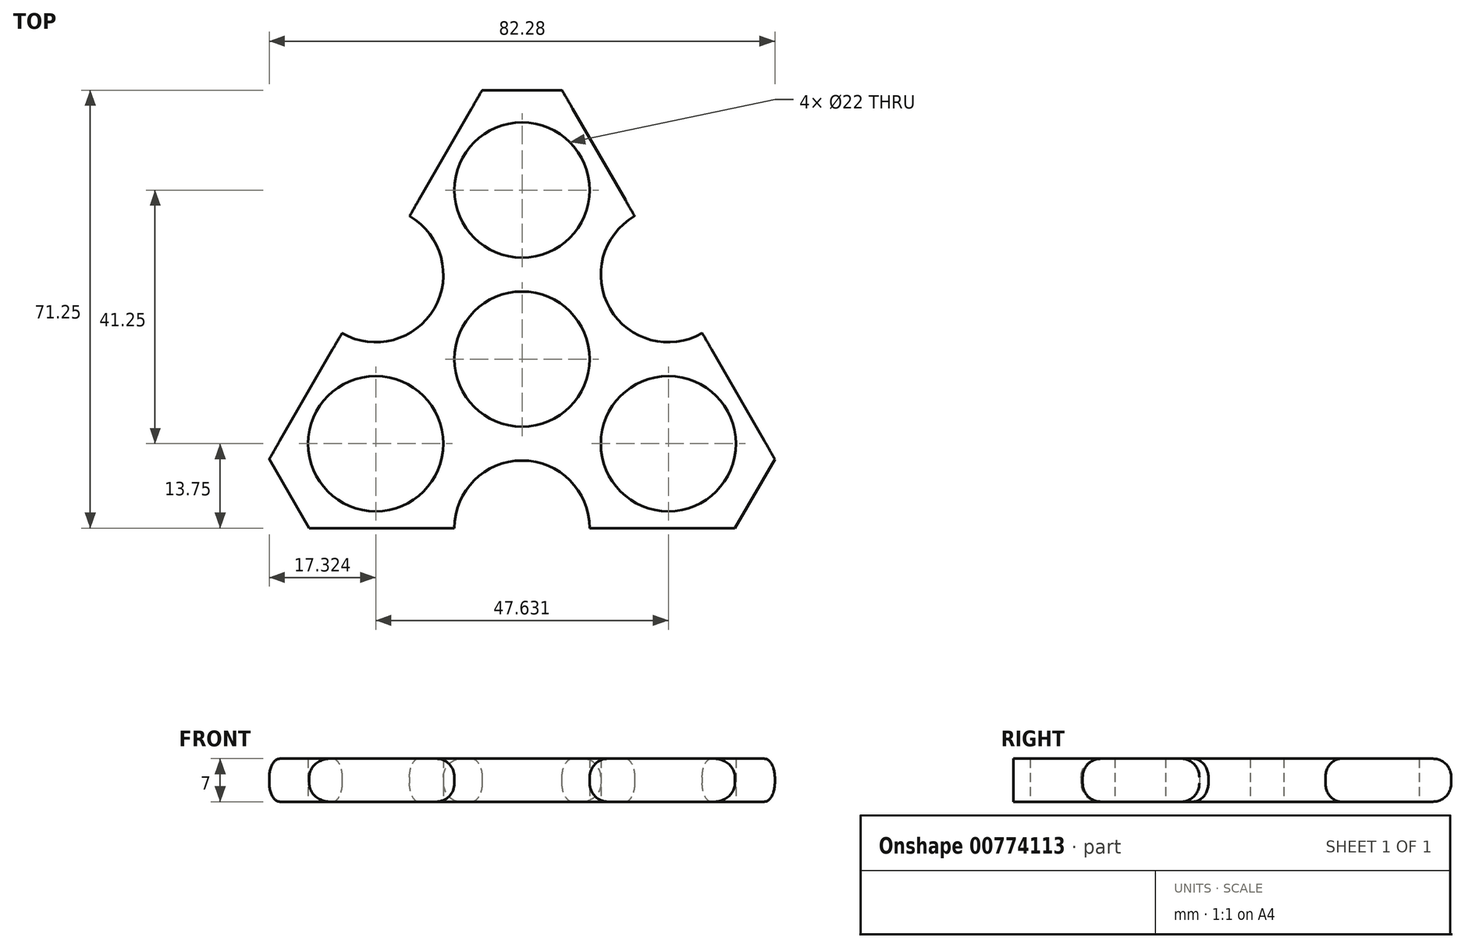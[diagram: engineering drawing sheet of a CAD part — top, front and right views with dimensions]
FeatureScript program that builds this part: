
annotation { "Feature Type Name" : "Feature", "Feature Type Description" : "" }
export const myFeature = defineFeature(function(context is Context, id is Id, definition is map)
    precondition{}
    {
        {
            var Q0;
            Q0=qCreatedBy(makeId("Top.planeOp"),FACE);
            var sketch = newSketch(context, id + "F0", { "sketchPlane" : qUnion([Q0])});
            skPoint(sketch, "E0", {"position": v(0, 0) * mm});
            skCircle(sketch, "E1", {"center": v(0, 0) * mm, "radius": 11 * mm});
            skCircle(sketch, "E2.cCircle", {"center": v(0, 0) * mm, "radius": 27.5 * mm, "construction": true});
            skLineSegment(sketch, "E2.0", {"start": v(47.63, -27.5) * mm, "end": v(-47.63, -27.5) * mm});
            skLineSegment(sketch, "E2.1", {"start": v(-47.63, -27.5) * mm, "end": v(0, 55) * mm});
            skLineSegment(sketch, "E2.2", {"start": v(0, 55) * mm, "end": v(47.63, -27.5) * mm});
            skPoint(sketch, "E2.0.midPoint", {"position": v(0, -27.5) * mm});
            skLineSegment(sketch, "E3", {"start": v(-47.63, -27.5) * mm, "end": v(0, 0) * mm});
            skLineSegment(sketch, "E4", {"start": v(0, 0) * mm, "end": v(47.63, -27.5) * mm});
            skLineSegment(sketch, "E5", {"start": v(0, 0) * mm, "end": v(0, 55) * mm});
            skCircle(sketch, "E6", {"center": v(-23.82, 13.75) * mm, "radius": 11 * mm});
            skCircle(sketch, "E7", {"center": v(23.82, 13.75) * mm, "radius": 11 * mm});
            skCircle(sketch, "E8", {"center": v(0, -27.5) * mm, "radius": 11 * mm});
            skPoint(sketch, "E9", {"position": v(23.82, -13.75) * mm});
            skPoint(sketch, "E10", {"position": v(0, 27.5) * mm});
            skPoint(sketch, "E11", {"position": v(-23.82, -13.75) * mm});
            skCircle(sketch, "E12", {"center": v(-23.82, -13.75) * mm, "radius": 11 * mm});
            skCircle(sketch, "E13", {"center": v(23.82, -13.75) * mm, "radius": 11 * mm});
            skCircle(sketch, "E14", {"center": v(0, 27.5) * mm, "radius": 11 * mm});
            skSolve(sketch);
        }
        {
            var Q0;
            {var subQ8=sQuery(id+"F0.wireOp",EDGE,"E3");var subQ11=sQuery(id+"F0.wireOp",EDGE,"E1");var subQ12=makeQuery(id+"F0.imprint","INTERSECT",VERTEX,{"derivedFrom":[subQ11,subQ8]});Q0=makeQuery(id+"F0.imprint","IMPRINT",FACE,{"disambiguationData":[TD([[makeQuery(id+"F0.imprint","IMPRINT",EDGE,{"disambiguationData":[TD([[subQ12,1.0]])],"derivedFrom":subQ11}),-1.0]])]});}
            var Q1;
            {var subQ0=sQuery(id+"F0.wireOp",EDGE,"E5");var subQ4=sQuery(id+"F0.wireOp",EDGE,"E1");var subQ5=makeQuery(id+"F0.imprint","INTERSECT",VERTEX,{"derivedFrom":[subQ4,subQ0]});Q1=makeQuery(id+"F0.imprint","IMPRINT",FACE,{"disambiguationData":[TD([[makeQuery(id+"F0.imprint","IMPRINT",EDGE,{"disambiguationData":[TD([[subQ5,1.0]])],"derivedFrom":subQ4}),-1.0]])]});}
            var Q2;
            {var subQ8=sQuery(id+"F0.wireOp",EDGE,"E3");var subQ11=sQuery(id+"F0.wireOp",EDGE,"E1");var subQ12=makeQuery(id+"F0.imprint","INTERSECT",VERTEX,{"derivedFrom":[subQ11,subQ8]});Q2=makeQuery(id+"F0.imprint","IMPRINT",FACE,{"disambiguationData":[TD([[makeQuery(id+"F0.imprint","IMPRINT",EDGE,{"disambiguationData":[TD([[subQ12,-1.0]])],"derivedFrom":subQ11}),-1.0]])]});}
            extrude(context, id + "F1", {"entities" : qUnion([Q0, Q1, Q2]), "depth" : 3.5 * mm, "offsetDistance" : 25 * mm, "hasSecondDirection" : true, "secondDirectionOppositeDirection" : true, "secondDirectionDepth" : 3.5 * mm});
        }
        {
            var Q0;
            Q0=makeQuery(id+"F1.opExtrude","SWEPT_EDGE",EDGE,{"disambiguationData":[OSD([sQuery(id+"F0.wireOp",EDGE,"E2.1"),sQuery(id+"F0.wireOp",EDGE,"E2.2"),sQuery(id+"F0.wireOp",EDGE,"E5")])]});
            var Q1;
            Q1=makeQuery(id+"F1.opExtrude","SWEPT_EDGE",EDGE,{"disambiguationData":[OSD([sQuery(id+"F0.wireOp",EDGE,"E2.0"),sQuery(id+"F0.wireOp",EDGE,"E2.2"),sQuery(id+"F0.wireOp",EDGE,"E4")])]});
            var Q2;
            Q2=makeQuery(id+"F1.opExtrude","SWEPT_EDGE",EDGE,{"disambiguationData":[OSD([sQuery(id+"F0.wireOp",EDGE,"E2.0"),sQuery(id+"F0.wireOp",EDGE,"E2.1"),sQuery(id+"F0.wireOp",EDGE,"E3")])]});
            chamfer(context, id + "F2", {"entities" : qUnion([Q0, Q1, Q2]), "width" : 7.5 * mm, "tangentPropagation" : true});
        }
        {
            var Q0;
            {var subQ0=sQuery(id+"F0.wireOp",EDGE,"E2.2");Q0=makeQuery(id+"F1.opExtrude","CAP_EDGE",EDGE,{"disambiguationData":[OSD([subQ0]),TDD([makeQuery(id+"F0.imprint","IMPRINT",EDGE,{"disambiguationData":[TD([[makeQuery(id+"F0.imprint","INTERSECT",VERTEX,{"disambiguationData":[OD(0.0)],"derivedFrom":[subQ0,sQuery(id+"F0.wireOp",EDGE,"E7")]}),1.0]])],"derivedFrom":subQ0})])],"isStart":false});}
            var Q1;
            Q1=makeQuery(id+"F1.opExtrude","CAP_EDGE",EDGE,{"disambiguationData":[OSD([sQuery(id+"F0.wireOp",EDGE,"E7")])],"isStart":false});
            var Q2;
            {var subQ0=sQuery(id+"F0.wireOp",EDGE,"E2.2");Q2=makeQuery(id+"F1.opExtrude","CAP_EDGE",EDGE,{"disambiguationData":[OSD([subQ0]),TDD([makeQuery(id+"F0.imprint","IMPRINT",EDGE,{"disambiguationData":[TD([[makeQuery(id+"F0.imprint","INTERSECT",VERTEX,{"disambiguationData":[OD(1.0)],"derivedFrom":[subQ0,sQuery(id+"F0.wireOp",EDGE,"E7")]}),-1.0]])],"derivedFrom":subQ0})])],"isStart":false});}
            var Q3;
            {var subQ0=sQuery(id+"F0.wireOp",EDGE,"E2.2");var subQ1=sQuery(id+"F0.wireOp",EDGE,"E2.0");Q3=makeQuery(id+"F2.opChamfer","BLEND_EDGE",EDGE,{"blendedFrom":[makeQuery(id+"F1.opExtrude","SWEPT_EDGE",EDGE,{"disambiguationData":[OSD([subQ1,subQ0,sQuery(id+"F0.wireOp",EDGE,"E4")])]}),makeQuery(id+"F1.opExtrude","CAP_FACE",FACE,{"disambiguationData":[OSD([sQuery(id+"F0.wireOp",EDGE,"E1"),subQ1,sQuery(id+"F0.wireOp",EDGE,"E2.1"),subQ0,sQuery(id+"F0.wireOp",EDGE,"E6"),sQuery(id+"F0.wireOp",EDGE,"E7"),sQuery(id+"F0.wireOp",EDGE,"E8"),sQuery(id+"F0.wireOp",EDGE,"eb86181a-66c7-44a9-927e-2462891ccdc7.0"),sQuery(id+"F0.wireOp",EDGE,"eb86181a-66c7-44a9-927e-2462891ccdc7.1"),sQuery(id+"F0.wireOp",EDGE,"eb86181a-66c7-44a9-927e-2462891ccdc7.2"),sQuery(id+"F0.wireOp",EDGE,"eb86181a-66c7-44a9-927e-2462891ccdc7.3"),sQuery(id+"F0.wireOp",EDGE,"eb86181a-66c7-44a9-927e-2462891ccdc7.4"),sQuery(id+"F0.wireOp",EDGE,"eb86181a-66c7-44a9-927e-2462891ccdc7.5"),sQuery(id+"F0.wireOp",EDGE,"eff1ef34-f5c1-4426-bce6-d10491bb5129.0"),sQuery(id+"F0.wireOp",EDGE,"eff1ef34-f5c1-4426-bce6-d10491bb5129.1"),sQuery(id+"F0.wireOp",EDGE,"eff1ef34-f5c1-4426-bce6-d10491bb5129.2"),sQuery(id+"F0.wireOp",EDGE,"eff1ef34-f5c1-4426-bce6-d10491bb5129.3"),sQuery(id+"F0.wireOp",EDGE,"eff1ef34-f5c1-4426-bce6-d10491bb5129.4"),sQuery(id+"F0.wireOp",EDGE,"eff1ef34-f5c1-4426-bce6-d10491bb5129.5"),sQuery(id+"F0.wireOp",EDGE,"caa0a2bf-8681-4059-bf23-da4b8e81c40b0.MirrorCS"),sQuery(id+"F0.wireOp",EDGE,"1fd086fe-55f3-407d-936a-1a1085770df10.MirrorCS"),sQuery(id+"F0.wireOp",EDGE,"178d0676-7881-4249-8293-cbce84a7fd370.MirrorCS"),sQuery(id+"F0.wireOp",EDGE,"88477509-62b1-4317-9a81-a130adc69aff0.MirrorCS"),sQuery(id+"F0.wireOp",EDGE,"1c665bfd-ff3e-46d6-9b43-bc498a36d9eb0.MirrorCS"),sQuery(id+"F0.wireOp",EDGE,"5c9001ee-5b7d-4471-8c19-4e4f09c0f1da0.MirrorCS")])],"isStart":false})],"blendedInto":[makeQuery(id+"F1.opExtrude","CAP_FACE",FACE,{"disambiguationData":[OSD([sQuery(id+"F0.wireOp",EDGE,"E1"),subQ1,sQuery(id+"F0.wireOp",EDGE,"E2.1"),subQ0,sQuery(id+"F0.wireOp",EDGE,"E6"),sQuery(id+"F0.wireOp",EDGE,"E7"),sQuery(id+"F0.wireOp",EDGE,"E8"),sQuery(id+"F0.wireOp",EDGE,"eb86181a-66c7-44a9-927e-2462891ccdc7.0"),sQuery(id+"F0.wireOp",EDGE,"eb86181a-66c7-44a9-927e-2462891ccdc7.1"),sQuery(id+"F0.wireOp",EDGE,"eb86181a-66c7-44a9-927e-2462891ccdc7.2"),sQuery(id+"F0.wireOp",EDGE,"eb86181a-66c7-44a9-927e-2462891ccdc7.3"),sQuery(id+"F0.wireOp",EDGE,"eb86181a-66c7-44a9-927e-2462891ccdc7.4"),sQuery(id+"F0.wireOp",EDGE,"eb86181a-66c7-44a9-927e-2462891ccdc7.5"),sQuery(id+"F0.wireOp",EDGE,"eff1ef34-f5c1-4426-bce6-d10491bb5129.0"),sQuery(id+"F0.wireOp",EDGE,"eff1ef34-f5c1-4426-bce6-d10491bb5129.1"),sQuery(id+"F0.wireOp",EDGE,"eff1ef34-f5c1-4426-bce6-d10491bb5129.2"),sQuery(id+"F0.wireOp",EDGE,"eff1ef34-f5c1-4426-bce6-d10491bb5129.3"),sQuery(id+"F0.wireOp",EDGE,"eff1ef34-f5c1-4426-bce6-d10491bb5129.4"),sQuery(id+"F0.wireOp",EDGE,"eff1ef34-f5c1-4426-bce6-d10491bb5129.5"),sQuery(id+"F0.wireOp",EDGE,"caa0a2bf-8681-4059-bf23-da4b8e81c40b0.MirrorCS"),sQuery(id+"F0.wireOp",EDGE,"1fd086fe-55f3-407d-936a-1a1085770df10.MirrorCS"),sQuery(id+"F0.wireOp",EDGE,"178d0676-7881-4249-8293-cbce84a7fd370.MirrorCS"),sQuery(id+"F0.wireOp",EDGE,"88477509-62b1-4317-9a81-a130adc69aff0.MirrorCS"),sQuery(id+"F0.wireOp",EDGE,"1c665bfd-ff3e-46d6-9b43-bc498a36d9eb0.MirrorCS"),sQuery(id+"F0.wireOp",EDGE,"5c9001ee-5b7d-4471-8c19-4e4f09c0f1da0.MirrorCS")])],"isStart":false})]});}
            var Q4;
            {var subQ0=sQuery(id+"F0.wireOp",EDGE,"E2.0");Q4=makeQuery(id+"F1.opExtrude","CAP_EDGE",EDGE,{"disambiguationData":[OSD([subQ0]),TDD([makeQuery(id+"F0.imprint","IMPRINT",EDGE,{"disambiguationData":[TD([[makeQuery(id+"F0.imprint","INTERSECT",VERTEX,{"disambiguationData":[OD(0.0)],"derivedFrom":[subQ0,sQuery(id+"F0.wireOp",EDGE,"E8")]}),1.0]])],"derivedFrom":subQ0})])],"isStart":false});}
            var Q5;
            Q5=makeQuery(id+"F1.opExtrude","CAP_EDGE",EDGE,{"disambiguationData":[OSD([sQuery(id+"F0.wireOp",EDGE,"E8")])],"isStart":false});
            var Q6;
            {var subQ0=sQuery(id+"F0.wireOp",EDGE,"E2.0");Q6=makeQuery(id+"F1.opExtrude","CAP_EDGE",EDGE,{"disambiguationData":[OSD([subQ0]),TDD([makeQuery(id+"F0.imprint","IMPRINT",EDGE,{"disambiguationData":[TD([[makeQuery(id+"F0.imprint","INTERSECT",VERTEX,{"disambiguationData":[OD(1.0)],"derivedFrom":[subQ0,sQuery(id+"F0.wireOp",EDGE,"E8")]}),-1.0]])],"derivedFrom":subQ0})])],"isStart":false});}
            var Q7;
            {var subQ0=sQuery(id+"F0.wireOp",EDGE,"E2.1");var subQ1=sQuery(id+"F0.wireOp",EDGE,"E2.0");Q7=makeQuery(id+"F2.opChamfer","BLEND_EDGE",EDGE,{"blendedFrom":[makeQuery(id+"F1.opExtrude","SWEPT_EDGE",EDGE,{"disambiguationData":[OSD([subQ1,subQ0,sQuery(id+"F0.wireOp",EDGE,"E3")])]}),makeQuery(id+"F1.opExtrude","CAP_FACE",FACE,{"disambiguationData":[OSD([sQuery(id+"F0.wireOp",EDGE,"E1"),subQ1,subQ0,sQuery(id+"F0.wireOp",EDGE,"E2.2"),sQuery(id+"F0.wireOp",EDGE,"E6"),sQuery(id+"F0.wireOp",EDGE,"E7"),sQuery(id+"F0.wireOp",EDGE,"E8"),sQuery(id+"F0.wireOp",EDGE,"eb86181a-66c7-44a9-927e-2462891ccdc7.0"),sQuery(id+"F0.wireOp",EDGE,"eb86181a-66c7-44a9-927e-2462891ccdc7.1"),sQuery(id+"F0.wireOp",EDGE,"eb86181a-66c7-44a9-927e-2462891ccdc7.2"),sQuery(id+"F0.wireOp",EDGE,"eb86181a-66c7-44a9-927e-2462891ccdc7.3"),sQuery(id+"F0.wireOp",EDGE,"eb86181a-66c7-44a9-927e-2462891ccdc7.4"),sQuery(id+"F0.wireOp",EDGE,"eb86181a-66c7-44a9-927e-2462891ccdc7.5"),sQuery(id+"F0.wireOp",EDGE,"eff1ef34-f5c1-4426-bce6-d10491bb5129.0"),sQuery(id+"F0.wireOp",EDGE,"eff1ef34-f5c1-4426-bce6-d10491bb5129.1"),sQuery(id+"F0.wireOp",EDGE,"eff1ef34-f5c1-4426-bce6-d10491bb5129.2"),sQuery(id+"F0.wireOp",EDGE,"eff1ef34-f5c1-4426-bce6-d10491bb5129.3"),sQuery(id+"F0.wireOp",EDGE,"eff1ef34-f5c1-4426-bce6-d10491bb5129.4"),sQuery(id+"F0.wireOp",EDGE,"eff1ef34-f5c1-4426-bce6-d10491bb5129.5"),sQuery(id+"F0.wireOp",EDGE,"caa0a2bf-8681-4059-bf23-da4b8e81c40b0.MirrorCS"),sQuery(id+"F0.wireOp",EDGE,"1fd086fe-55f3-407d-936a-1a1085770df10.MirrorCS"),sQuery(id+"F0.wireOp",EDGE,"178d0676-7881-4249-8293-cbce84a7fd370.MirrorCS"),sQuery(id+"F0.wireOp",EDGE,"88477509-62b1-4317-9a81-a130adc69aff0.MirrorCS"),sQuery(id+"F0.wireOp",EDGE,"1c665bfd-ff3e-46d6-9b43-bc498a36d9eb0.MirrorCS"),sQuery(id+"F0.wireOp",EDGE,"5c9001ee-5b7d-4471-8c19-4e4f09c0f1da0.MirrorCS")])],"isStart":false})],"blendedInto":[makeQuery(id+"F1.opExtrude","CAP_FACE",FACE,{"disambiguationData":[OSD([sQuery(id+"F0.wireOp",EDGE,"E1"),subQ1,subQ0,sQuery(id+"F0.wireOp",EDGE,"E2.2"),sQuery(id+"F0.wireOp",EDGE,"E6"),sQuery(id+"F0.wireOp",EDGE,"E7"),sQuery(id+"F0.wireOp",EDGE,"E8"),sQuery(id+"F0.wireOp",EDGE,"eb86181a-66c7-44a9-927e-2462891ccdc7.0"),sQuery(id+"F0.wireOp",EDGE,"eb86181a-66c7-44a9-927e-2462891ccdc7.1"),sQuery(id+"F0.wireOp",EDGE,"eb86181a-66c7-44a9-927e-2462891ccdc7.2"),sQuery(id+"F0.wireOp",EDGE,"eb86181a-66c7-44a9-927e-2462891ccdc7.3"),sQuery(id+"F0.wireOp",EDGE,"eb86181a-66c7-44a9-927e-2462891ccdc7.4"),sQuery(id+"F0.wireOp",EDGE,"eb86181a-66c7-44a9-927e-2462891ccdc7.5"),sQuery(id+"F0.wireOp",EDGE,"eff1ef34-f5c1-4426-bce6-d10491bb5129.0"),sQuery(id+"F0.wireOp",EDGE,"eff1ef34-f5c1-4426-bce6-d10491bb5129.1"),sQuery(id+"F0.wireOp",EDGE,"eff1ef34-f5c1-4426-bce6-d10491bb5129.2"),sQuery(id+"F0.wireOp",EDGE,"eff1ef34-f5c1-4426-bce6-d10491bb5129.3"),sQuery(id+"F0.wireOp",EDGE,"eff1ef34-f5c1-4426-bce6-d10491bb5129.4"),sQuery(id+"F0.wireOp",EDGE,"eff1ef34-f5c1-4426-bce6-d10491bb5129.5"),sQuery(id+"F0.wireOp",EDGE,"caa0a2bf-8681-4059-bf23-da4b8e81c40b0.MirrorCS"),sQuery(id+"F0.wireOp",EDGE,"1fd086fe-55f3-407d-936a-1a1085770df10.MirrorCS"),sQuery(id+"F0.wireOp",EDGE,"178d0676-7881-4249-8293-cbce84a7fd370.MirrorCS"),sQuery(id+"F0.wireOp",EDGE,"88477509-62b1-4317-9a81-a130adc69aff0.MirrorCS"),sQuery(id+"F0.wireOp",EDGE,"1c665bfd-ff3e-46d6-9b43-bc498a36d9eb0.MirrorCS"),sQuery(id+"F0.wireOp",EDGE,"5c9001ee-5b7d-4471-8c19-4e4f09c0f1da0.MirrorCS")])],"isStart":false})]});}
            var Q8;
            {var subQ0=sQuery(id+"F0.wireOp",EDGE,"E2.1");Q8=makeQuery(id+"F1.opExtrude","CAP_EDGE",EDGE,{"disambiguationData":[OSD([subQ0]),TDD([makeQuery(id+"F0.imprint","IMPRINT",EDGE,{"disambiguationData":[TD([[makeQuery(id+"F0.imprint","INTERSECT",VERTEX,{"disambiguationData":[OD(0.0)],"derivedFrom":[subQ0,sQuery(id+"F0.wireOp",EDGE,"E6")]}),1.0]])],"derivedFrom":subQ0})])],"isStart":false});}
            var Q9;
            Q9=makeQuery(id+"F1.opExtrude","CAP_EDGE",EDGE,{"disambiguationData":[OSD([sQuery(id+"F0.wireOp",EDGE,"E6")])],"isStart":false});
            var Q10;
            {var subQ0=sQuery(id+"F0.wireOp",EDGE,"E2.1");Q10=makeQuery(id+"F1.opExtrude","CAP_EDGE",EDGE,{"disambiguationData":[OSD([subQ0]),TDD([makeQuery(id+"F0.imprint","IMPRINT",EDGE,{"disambiguationData":[TD([[makeQuery(id+"F0.imprint","INTERSECT",VERTEX,{"disambiguationData":[OD(1.0)],"derivedFrom":[subQ0,sQuery(id+"F0.wireOp",EDGE,"E6")]}),-1.0]])],"derivedFrom":subQ0})])],"isStart":false});}
            var Q11;
            {var subQ0=sQuery(id+"F0.wireOp",EDGE,"E2.2");var subQ1=sQuery(id+"F0.wireOp",EDGE,"E2.1");Q11=makeQuery(id+"F2.opChamfer","BLEND_EDGE",EDGE,{"blendedFrom":[makeQuery(id+"F1.opExtrude","SWEPT_EDGE",EDGE,{"disambiguationData":[OSD([subQ1,subQ0,sQuery(id+"F0.wireOp",EDGE,"E5")])]}),makeQuery(id+"F1.opExtrude","CAP_FACE",FACE,{"disambiguationData":[OSD([sQuery(id+"F0.wireOp",EDGE,"E1"),sQuery(id+"F0.wireOp",EDGE,"E2.0"),subQ1,subQ0,sQuery(id+"F0.wireOp",EDGE,"E6"),sQuery(id+"F0.wireOp",EDGE,"E7"),sQuery(id+"F0.wireOp",EDGE,"E8"),sQuery(id+"F0.wireOp",EDGE,"eb86181a-66c7-44a9-927e-2462891ccdc7.0"),sQuery(id+"F0.wireOp",EDGE,"eb86181a-66c7-44a9-927e-2462891ccdc7.1"),sQuery(id+"F0.wireOp",EDGE,"eb86181a-66c7-44a9-927e-2462891ccdc7.2"),sQuery(id+"F0.wireOp",EDGE,"eb86181a-66c7-44a9-927e-2462891ccdc7.3"),sQuery(id+"F0.wireOp",EDGE,"eb86181a-66c7-44a9-927e-2462891ccdc7.4"),sQuery(id+"F0.wireOp",EDGE,"eb86181a-66c7-44a9-927e-2462891ccdc7.5"),sQuery(id+"F0.wireOp",EDGE,"eff1ef34-f5c1-4426-bce6-d10491bb5129.0"),sQuery(id+"F0.wireOp",EDGE,"eff1ef34-f5c1-4426-bce6-d10491bb5129.1"),sQuery(id+"F0.wireOp",EDGE,"eff1ef34-f5c1-4426-bce6-d10491bb5129.2"),sQuery(id+"F0.wireOp",EDGE,"eff1ef34-f5c1-4426-bce6-d10491bb5129.3"),sQuery(id+"F0.wireOp",EDGE,"eff1ef34-f5c1-4426-bce6-d10491bb5129.4"),sQuery(id+"F0.wireOp",EDGE,"eff1ef34-f5c1-4426-bce6-d10491bb5129.5"),sQuery(id+"F0.wireOp",EDGE,"caa0a2bf-8681-4059-bf23-da4b8e81c40b0.MirrorCS"),sQuery(id+"F0.wireOp",EDGE,"1fd086fe-55f3-407d-936a-1a1085770df10.MirrorCS"),sQuery(id+"F0.wireOp",EDGE,"178d0676-7881-4249-8293-cbce84a7fd370.MirrorCS"),sQuery(id+"F0.wireOp",EDGE,"88477509-62b1-4317-9a81-a130adc69aff0.MirrorCS"),sQuery(id+"F0.wireOp",EDGE,"1c665bfd-ff3e-46d6-9b43-bc498a36d9eb0.MirrorCS"),sQuery(id+"F0.wireOp",EDGE,"5c9001ee-5b7d-4471-8c19-4e4f09c0f1da0.MirrorCS")])],"isStart":false})],"blendedInto":[makeQuery(id+"F1.opExtrude","CAP_FACE",FACE,{"disambiguationData":[OSD([sQuery(id+"F0.wireOp",EDGE,"E1"),sQuery(id+"F0.wireOp",EDGE,"E2.0"),subQ1,subQ0,sQuery(id+"F0.wireOp",EDGE,"E6"),sQuery(id+"F0.wireOp",EDGE,"E7"),sQuery(id+"F0.wireOp",EDGE,"E8"),sQuery(id+"F0.wireOp",EDGE,"eb86181a-66c7-44a9-927e-2462891ccdc7.0"),sQuery(id+"F0.wireOp",EDGE,"eb86181a-66c7-44a9-927e-2462891ccdc7.1"),sQuery(id+"F0.wireOp",EDGE,"eb86181a-66c7-44a9-927e-2462891ccdc7.2"),sQuery(id+"F0.wireOp",EDGE,"eb86181a-66c7-44a9-927e-2462891ccdc7.3"),sQuery(id+"F0.wireOp",EDGE,"eb86181a-66c7-44a9-927e-2462891ccdc7.4"),sQuery(id+"F0.wireOp",EDGE,"eb86181a-66c7-44a9-927e-2462891ccdc7.5"),sQuery(id+"F0.wireOp",EDGE,"eff1ef34-f5c1-4426-bce6-d10491bb5129.0"),sQuery(id+"F0.wireOp",EDGE,"eff1ef34-f5c1-4426-bce6-d10491bb5129.1"),sQuery(id+"F0.wireOp",EDGE,"eff1ef34-f5c1-4426-bce6-d10491bb5129.2"),sQuery(id+"F0.wireOp",EDGE,"eff1ef34-f5c1-4426-bce6-d10491bb5129.3"),sQuery(id+"F0.wireOp",EDGE,"eff1ef34-f5c1-4426-bce6-d10491bb5129.4"),sQuery(id+"F0.wireOp",EDGE,"eff1ef34-f5c1-4426-bce6-d10491bb5129.5"),sQuery(id+"F0.wireOp",EDGE,"caa0a2bf-8681-4059-bf23-da4b8e81c40b0.MirrorCS"),sQuery(id+"F0.wireOp",EDGE,"1fd086fe-55f3-407d-936a-1a1085770df10.MirrorCS"),sQuery(id+"F0.wireOp",EDGE,"178d0676-7881-4249-8293-cbce84a7fd370.MirrorCS"),sQuery(id+"F0.wireOp",EDGE,"88477509-62b1-4317-9a81-a130adc69aff0.MirrorCS"),sQuery(id+"F0.wireOp",EDGE,"1c665bfd-ff3e-46d6-9b43-bc498a36d9eb0.MirrorCS"),sQuery(id+"F0.wireOp",EDGE,"5c9001ee-5b7d-4471-8c19-4e4f09c0f1da0.MirrorCS")])],"isStart":false})]});}
            fillet(context, id + "F3", {"entities" : qUnion([Q0, Q1, Q2, Q3, Q4, Q5, Q6, Q7, Q8, Q9, Q10, Q11]), "radius" : 3 * mm, "tangentPropagation" : true, "allowEdgeOverflow" : false});
        }
        {
            var Q0;
            {var subQ0=sQuery(id+"F0.wireOp",EDGE,"E2.1");var subQ1=sQuery(id+"F0.wireOp",EDGE,"E2.0");Q0=makeQuery(id+"F2.opChamfer","BLEND_EDGE",EDGE,{"blendedFrom":[makeQuery(id+"F1.opExtrude","SWEPT_EDGE",EDGE,{"disambiguationData":[OSD([subQ1,subQ0,sQuery(id+"F0.wireOp",EDGE,"E3")])]}),makeQuery(id+"F1.opExtrude","CAP_FACE",FACE,{"disambiguationData":[OSD([sQuery(id+"F0.wireOp",EDGE,"E1"),subQ1,subQ0,sQuery(id+"F0.wireOp",EDGE,"E2.2"),sQuery(id+"F0.wireOp",EDGE,"E6"),sQuery(id+"F0.wireOp",EDGE,"E7"),sQuery(id+"F0.wireOp",EDGE,"E8"),sQuery(id+"F0.wireOp",EDGE,"eb86181a-66c7-44a9-927e-2462891ccdc7.0"),sQuery(id+"F0.wireOp",EDGE,"eb86181a-66c7-44a9-927e-2462891ccdc7.1"),sQuery(id+"F0.wireOp",EDGE,"eb86181a-66c7-44a9-927e-2462891ccdc7.2"),sQuery(id+"F0.wireOp",EDGE,"eb86181a-66c7-44a9-927e-2462891ccdc7.3"),sQuery(id+"F0.wireOp",EDGE,"eb86181a-66c7-44a9-927e-2462891ccdc7.4"),sQuery(id+"F0.wireOp",EDGE,"eb86181a-66c7-44a9-927e-2462891ccdc7.5"),sQuery(id+"F0.wireOp",EDGE,"eff1ef34-f5c1-4426-bce6-d10491bb5129.0"),sQuery(id+"F0.wireOp",EDGE,"eff1ef34-f5c1-4426-bce6-d10491bb5129.1"),sQuery(id+"F0.wireOp",EDGE,"eff1ef34-f5c1-4426-bce6-d10491bb5129.2"),sQuery(id+"F0.wireOp",EDGE,"eff1ef34-f5c1-4426-bce6-d10491bb5129.3"),sQuery(id+"F0.wireOp",EDGE,"eff1ef34-f5c1-4426-bce6-d10491bb5129.4"),sQuery(id+"F0.wireOp",EDGE,"eff1ef34-f5c1-4426-bce6-d10491bb5129.5"),sQuery(id+"F0.wireOp",EDGE,"caa0a2bf-8681-4059-bf23-da4b8e81c40b0.MirrorCS"),sQuery(id+"F0.wireOp",EDGE,"1fd086fe-55f3-407d-936a-1a1085770df10.MirrorCS"),sQuery(id+"F0.wireOp",EDGE,"178d0676-7881-4249-8293-cbce84a7fd370.MirrorCS"),sQuery(id+"F0.wireOp",EDGE,"88477509-62b1-4317-9a81-a130adc69aff0.MirrorCS"),sQuery(id+"F0.wireOp",EDGE,"1c665bfd-ff3e-46d6-9b43-bc498a36d9eb0.MirrorCS"),sQuery(id+"F0.wireOp",EDGE,"5c9001ee-5b7d-4471-8c19-4e4f09c0f1da0.MirrorCS")])],"isStart":true})],"blendedInto":[makeQuery(id+"F1.opExtrude","CAP_FACE",FACE,{"disambiguationData":[OSD([sQuery(id+"F0.wireOp",EDGE,"E1"),subQ1,subQ0,sQuery(id+"F0.wireOp",EDGE,"E2.2"),sQuery(id+"F0.wireOp",EDGE,"E6"),sQuery(id+"F0.wireOp",EDGE,"E7"),sQuery(id+"F0.wireOp",EDGE,"E8"),sQuery(id+"F0.wireOp",EDGE,"eb86181a-66c7-44a9-927e-2462891ccdc7.0"),sQuery(id+"F0.wireOp",EDGE,"eb86181a-66c7-44a9-927e-2462891ccdc7.1"),sQuery(id+"F0.wireOp",EDGE,"eb86181a-66c7-44a9-927e-2462891ccdc7.2"),sQuery(id+"F0.wireOp",EDGE,"eb86181a-66c7-44a9-927e-2462891ccdc7.3"),sQuery(id+"F0.wireOp",EDGE,"eb86181a-66c7-44a9-927e-2462891ccdc7.4"),sQuery(id+"F0.wireOp",EDGE,"eb86181a-66c7-44a9-927e-2462891ccdc7.5"),sQuery(id+"F0.wireOp",EDGE,"eff1ef34-f5c1-4426-bce6-d10491bb5129.0"),sQuery(id+"F0.wireOp",EDGE,"eff1ef34-f5c1-4426-bce6-d10491bb5129.1"),sQuery(id+"F0.wireOp",EDGE,"eff1ef34-f5c1-4426-bce6-d10491bb5129.2"),sQuery(id+"F0.wireOp",EDGE,"eff1ef34-f5c1-4426-bce6-d10491bb5129.3"),sQuery(id+"F0.wireOp",EDGE,"eff1ef34-f5c1-4426-bce6-d10491bb5129.4"),sQuery(id+"F0.wireOp",EDGE,"eff1ef34-f5c1-4426-bce6-d10491bb5129.5"),sQuery(id+"F0.wireOp",EDGE,"caa0a2bf-8681-4059-bf23-da4b8e81c40b0.MirrorCS"),sQuery(id+"F0.wireOp",EDGE,"1fd086fe-55f3-407d-936a-1a1085770df10.MirrorCS"),sQuery(id+"F0.wireOp",EDGE,"178d0676-7881-4249-8293-cbce84a7fd370.MirrorCS"),sQuery(id+"F0.wireOp",EDGE,"88477509-62b1-4317-9a81-a130adc69aff0.MirrorCS"),sQuery(id+"F0.wireOp",EDGE,"1c665bfd-ff3e-46d6-9b43-bc498a36d9eb0.MirrorCS"),sQuery(id+"F0.wireOp",EDGE,"5c9001ee-5b7d-4471-8c19-4e4f09c0f1da0.MirrorCS")])],"isStart":true})]});}
            var Q1;
            {var subQ0=sQuery(id+"F0.wireOp",EDGE,"E2.2");var subQ1=sQuery(id+"F0.wireOp",EDGE,"E2.0");Q1=makeQuery(id+"F2.opChamfer","BLEND_EDGE",EDGE,{"blendedFrom":[makeQuery(id+"F1.opExtrude","SWEPT_EDGE",EDGE,{"disambiguationData":[OSD([subQ1,subQ0,sQuery(id+"F0.wireOp",EDGE,"E4")])]}),makeQuery(id+"F1.opExtrude","CAP_FACE",FACE,{"disambiguationData":[OSD([sQuery(id+"F0.wireOp",EDGE,"E1"),subQ1,sQuery(id+"F0.wireOp",EDGE,"E2.1"),subQ0,sQuery(id+"F0.wireOp",EDGE,"E6"),sQuery(id+"F0.wireOp",EDGE,"E7"),sQuery(id+"F0.wireOp",EDGE,"E8"),sQuery(id+"F0.wireOp",EDGE,"eb86181a-66c7-44a9-927e-2462891ccdc7.0"),sQuery(id+"F0.wireOp",EDGE,"eb86181a-66c7-44a9-927e-2462891ccdc7.1"),sQuery(id+"F0.wireOp",EDGE,"eb86181a-66c7-44a9-927e-2462891ccdc7.2"),sQuery(id+"F0.wireOp",EDGE,"eb86181a-66c7-44a9-927e-2462891ccdc7.3"),sQuery(id+"F0.wireOp",EDGE,"eb86181a-66c7-44a9-927e-2462891ccdc7.4"),sQuery(id+"F0.wireOp",EDGE,"eb86181a-66c7-44a9-927e-2462891ccdc7.5"),sQuery(id+"F0.wireOp",EDGE,"eff1ef34-f5c1-4426-bce6-d10491bb5129.0"),sQuery(id+"F0.wireOp",EDGE,"eff1ef34-f5c1-4426-bce6-d10491bb5129.1"),sQuery(id+"F0.wireOp",EDGE,"eff1ef34-f5c1-4426-bce6-d10491bb5129.2"),sQuery(id+"F0.wireOp",EDGE,"eff1ef34-f5c1-4426-bce6-d10491bb5129.3"),sQuery(id+"F0.wireOp",EDGE,"eff1ef34-f5c1-4426-bce6-d10491bb5129.4"),sQuery(id+"F0.wireOp",EDGE,"eff1ef34-f5c1-4426-bce6-d10491bb5129.5"),sQuery(id+"F0.wireOp",EDGE,"caa0a2bf-8681-4059-bf23-da4b8e81c40b0.MirrorCS"),sQuery(id+"F0.wireOp",EDGE,"1fd086fe-55f3-407d-936a-1a1085770df10.MirrorCS"),sQuery(id+"F0.wireOp",EDGE,"178d0676-7881-4249-8293-cbce84a7fd370.MirrorCS"),sQuery(id+"F0.wireOp",EDGE,"88477509-62b1-4317-9a81-a130adc69aff0.MirrorCS"),sQuery(id+"F0.wireOp",EDGE,"1c665bfd-ff3e-46d6-9b43-bc498a36d9eb0.MirrorCS"),sQuery(id+"F0.wireOp",EDGE,"5c9001ee-5b7d-4471-8c19-4e4f09c0f1da0.MirrorCS")])],"isStart":true})],"blendedInto":[makeQuery(id+"F1.opExtrude","CAP_FACE",FACE,{"disambiguationData":[OSD([sQuery(id+"F0.wireOp",EDGE,"E1"),subQ1,sQuery(id+"F0.wireOp",EDGE,"E2.1"),subQ0,sQuery(id+"F0.wireOp",EDGE,"E6"),sQuery(id+"F0.wireOp",EDGE,"E7"),sQuery(id+"F0.wireOp",EDGE,"E8"),sQuery(id+"F0.wireOp",EDGE,"eb86181a-66c7-44a9-927e-2462891ccdc7.0"),sQuery(id+"F0.wireOp",EDGE,"eb86181a-66c7-44a9-927e-2462891ccdc7.1"),sQuery(id+"F0.wireOp",EDGE,"eb86181a-66c7-44a9-927e-2462891ccdc7.2"),sQuery(id+"F0.wireOp",EDGE,"eb86181a-66c7-44a9-927e-2462891ccdc7.3"),sQuery(id+"F0.wireOp",EDGE,"eb86181a-66c7-44a9-927e-2462891ccdc7.4"),sQuery(id+"F0.wireOp",EDGE,"eb86181a-66c7-44a9-927e-2462891ccdc7.5"),sQuery(id+"F0.wireOp",EDGE,"eff1ef34-f5c1-4426-bce6-d10491bb5129.0"),sQuery(id+"F0.wireOp",EDGE,"eff1ef34-f5c1-4426-bce6-d10491bb5129.1"),sQuery(id+"F0.wireOp",EDGE,"eff1ef34-f5c1-4426-bce6-d10491bb5129.2"),sQuery(id+"F0.wireOp",EDGE,"eff1ef34-f5c1-4426-bce6-d10491bb5129.3"),sQuery(id+"F0.wireOp",EDGE,"eff1ef34-f5c1-4426-bce6-d10491bb5129.4"),sQuery(id+"F0.wireOp",EDGE,"eff1ef34-f5c1-4426-bce6-d10491bb5129.5"),sQuery(id+"F0.wireOp",EDGE,"caa0a2bf-8681-4059-bf23-da4b8e81c40b0.MirrorCS"),sQuery(id+"F0.wireOp",EDGE,"1fd086fe-55f3-407d-936a-1a1085770df10.MirrorCS"),sQuery(id+"F0.wireOp",EDGE,"178d0676-7881-4249-8293-cbce84a7fd370.MirrorCS"),sQuery(id+"F0.wireOp",EDGE,"88477509-62b1-4317-9a81-a130adc69aff0.MirrorCS"),sQuery(id+"F0.wireOp",EDGE,"1c665bfd-ff3e-46d6-9b43-bc498a36d9eb0.MirrorCS"),sQuery(id+"F0.wireOp",EDGE,"5c9001ee-5b7d-4471-8c19-4e4f09c0f1da0.MirrorCS")])],"isStart":true})]});}
            var Q2;
            {var subQ0=sQuery(id+"F0.wireOp",EDGE,"E2.2");var subQ1=sQuery(id+"F0.wireOp",EDGE,"E2.1");Q2=makeQuery(id+"F2.opChamfer","BLEND_EDGE",EDGE,{"blendedFrom":[makeQuery(id+"F1.opExtrude","SWEPT_EDGE",EDGE,{"disambiguationData":[OSD([subQ1,subQ0,sQuery(id+"F0.wireOp",EDGE,"E5")])]}),makeQuery(id+"F1.opExtrude","CAP_FACE",FACE,{"disambiguationData":[OSD([sQuery(id+"F0.wireOp",EDGE,"E1"),sQuery(id+"F0.wireOp",EDGE,"E2.0"),subQ1,subQ0,sQuery(id+"F0.wireOp",EDGE,"E6"),sQuery(id+"F0.wireOp",EDGE,"E7"),sQuery(id+"F0.wireOp",EDGE,"E8"),sQuery(id+"F0.wireOp",EDGE,"eb86181a-66c7-44a9-927e-2462891ccdc7.0"),sQuery(id+"F0.wireOp",EDGE,"eb86181a-66c7-44a9-927e-2462891ccdc7.1"),sQuery(id+"F0.wireOp",EDGE,"eb86181a-66c7-44a9-927e-2462891ccdc7.2"),sQuery(id+"F0.wireOp",EDGE,"eb86181a-66c7-44a9-927e-2462891ccdc7.3"),sQuery(id+"F0.wireOp",EDGE,"eb86181a-66c7-44a9-927e-2462891ccdc7.4"),sQuery(id+"F0.wireOp",EDGE,"eb86181a-66c7-44a9-927e-2462891ccdc7.5"),sQuery(id+"F0.wireOp",EDGE,"eff1ef34-f5c1-4426-bce6-d10491bb5129.0"),sQuery(id+"F0.wireOp",EDGE,"eff1ef34-f5c1-4426-bce6-d10491bb5129.1"),sQuery(id+"F0.wireOp",EDGE,"eff1ef34-f5c1-4426-bce6-d10491bb5129.2"),sQuery(id+"F0.wireOp",EDGE,"eff1ef34-f5c1-4426-bce6-d10491bb5129.3"),sQuery(id+"F0.wireOp",EDGE,"eff1ef34-f5c1-4426-bce6-d10491bb5129.4"),sQuery(id+"F0.wireOp",EDGE,"eff1ef34-f5c1-4426-bce6-d10491bb5129.5"),sQuery(id+"F0.wireOp",EDGE,"caa0a2bf-8681-4059-bf23-da4b8e81c40b0.MirrorCS"),sQuery(id+"F0.wireOp",EDGE,"1fd086fe-55f3-407d-936a-1a1085770df10.MirrorCS"),sQuery(id+"F0.wireOp",EDGE,"178d0676-7881-4249-8293-cbce84a7fd370.MirrorCS"),sQuery(id+"F0.wireOp",EDGE,"88477509-62b1-4317-9a81-a130adc69aff0.MirrorCS"),sQuery(id+"F0.wireOp",EDGE,"1c665bfd-ff3e-46d6-9b43-bc498a36d9eb0.MirrorCS"),sQuery(id+"F0.wireOp",EDGE,"5c9001ee-5b7d-4471-8c19-4e4f09c0f1da0.MirrorCS")])],"isStart":true})],"blendedInto":[makeQuery(id+"F1.opExtrude","CAP_FACE",FACE,{"disambiguationData":[OSD([sQuery(id+"F0.wireOp",EDGE,"E1"),sQuery(id+"F0.wireOp",EDGE,"E2.0"),subQ1,subQ0,sQuery(id+"F0.wireOp",EDGE,"E6"),sQuery(id+"F0.wireOp",EDGE,"E7"),sQuery(id+"F0.wireOp",EDGE,"E8"),sQuery(id+"F0.wireOp",EDGE,"eb86181a-66c7-44a9-927e-2462891ccdc7.0"),sQuery(id+"F0.wireOp",EDGE,"eb86181a-66c7-44a9-927e-2462891ccdc7.1"),sQuery(id+"F0.wireOp",EDGE,"eb86181a-66c7-44a9-927e-2462891ccdc7.2"),sQuery(id+"F0.wireOp",EDGE,"eb86181a-66c7-44a9-927e-2462891ccdc7.3"),sQuery(id+"F0.wireOp",EDGE,"eb86181a-66c7-44a9-927e-2462891ccdc7.4"),sQuery(id+"F0.wireOp",EDGE,"eb86181a-66c7-44a9-927e-2462891ccdc7.5"),sQuery(id+"F0.wireOp",EDGE,"eff1ef34-f5c1-4426-bce6-d10491bb5129.0"),sQuery(id+"F0.wireOp",EDGE,"eff1ef34-f5c1-4426-bce6-d10491bb5129.1"),sQuery(id+"F0.wireOp",EDGE,"eff1ef34-f5c1-4426-bce6-d10491bb5129.2"),sQuery(id+"F0.wireOp",EDGE,"eff1ef34-f5c1-4426-bce6-d10491bb5129.3"),sQuery(id+"F0.wireOp",EDGE,"eff1ef34-f5c1-4426-bce6-d10491bb5129.4"),sQuery(id+"F0.wireOp",EDGE,"eff1ef34-f5c1-4426-bce6-d10491bb5129.5"),sQuery(id+"F0.wireOp",EDGE,"caa0a2bf-8681-4059-bf23-da4b8e81c40b0.MirrorCS"),sQuery(id+"F0.wireOp",EDGE,"1fd086fe-55f3-407d-936a-1a1085770df10.MirrorCS"),sQuery(id+"F0.wireOp",EDGE,"178d0676-7881-4249-8293-cbce84a7fd370.MirrorCS"),sQuery(id+"F0.wireOp",EDGE,"88477509-62b1-4317-9a81-a130adc69aff0.MirrorCS"),sQuery(id+"F0.wireOp",EDGE,"1c665bfd-ff3e-46d6-9b43-bc498a36d9eb0.MirrorCS"),sQuery(id+"F0.wireOp",EDGE,"5c9001ee-5b7d-4471-8c19-4e4f09c0f1da0.MirrorCS")])],"isStart":true})]});}
            var Q3;
            {var subQ0=sQuery(id+"F0.wireOp",EDGE,"E2.1");Q3=makeQuery(id+"F1.opExtrude","CAP_EDGE",EDGE,{"disambiguationData":[OSD([subQ0]),TDD([makeQuery(id+"F0.imprint","IMPRINT",EDGE,{"disambiguationData":[TD([[makeQuery(id+"F0.imprint","INTERSECT",VERTEX,{"disambiguationData":[OD(1.0)],"derivedFrom":[subQ0,sQuery(id+"F0.wireOp",EDGE,"E6")]}),-1.0]])],"derivedFrom":subQ0})])],"isStart":true});}
            var Q4;
            Q4=makeQuery(id+"F1.opExtrude","CAP_EDGE",EDGE,{"disambiguationData":[OSD([sQuery(id+"F0.wireOp",EDGE,"E6")])],"isStart":true});
            var Q5;
            {var subQ0=sQuery(id+"F0.wireOp",EDGE,"E2.1");Q5=makeQuery(id+"F1.opExtrude","CAP_EDGE",EDGE,{"disambiguationData":[OSD([subQ0]),TDD([makeQuery(id+"F0.imprint","IMPRINT",EDGE,{"disambiguationData":[TD([[makeQuery(id+"F0.imprint","INTERSECT",VERTEX,{"disambiguationData":[OD(0.0)],"derivedFrom":[subQ0,sQuery(id+"F0.wireOp",EDGE,"E6")]}),1.0]])],"derivedFrom":subQ0})])],"isStart":true});}
            var Q6;
            {var subQ0=sQuery(id+"F0.wireOp",EDGE,"E2.0");Q6=makeQuery(id+"F1.opExtrude","CAP_EDGE",EDGE,{"disambiguationData":[OSD([subQ0]),TDD([makeQuery(id+"F0.imprint","IMPRINT",EDGE,{"disambiguationData":[TD([[makeQuery(id+"F0.imprint","INTERSECT",VERTEX,{"disambiguationData":[OD(1.0)],"derivedFrom":[subQ0,sQuery(id+"F0.wireOp",EDGE,"E8")]}),-1.0]])],"derivedFrom":subQ0})])],"isStart":true});}
            var Q7;
            Q7=makeQuery(id+"F1.opExtrude","CAP_EDGE",EDGE,{"disambiguationData":[OSD([sQuery(id+"F0.wireOp",EDGE,"E8")])],"isStart":true});
            var Q8;
            {var subQ0=sQuery(id+"F0.wireOp",EDGE,"E2.0");Q8=makeQuery(id+"F1.opExtrude","CAP_EDGE",EDGE,{"disambiguationData":[OSD([subQ0]),TDD([makeQuery(id+"F0.imprint","IMPRINT",EDGE,{"disambiguationData":[TD([[makeQuery(id+"F0.imprint","INTERSECT",VERTEX,{"disambiguationData":[OD(0.0)],"derivedFrom":[subQ0,sQuery(id+"F0.wireOp",EDGE,"E8")]}),1.0]])],"derivedFrom":subQ0})])],"isStart":true});}
            var Q9;
            {var subQ0=sQuery(id+"F0.wireOp",EDGE,"E2.2");Q9=makeQuery(id+"F1.opExtrude","CAP_EDGE",EDGE,{"disambiguationData":[OSD([subQ0]),TDD([makeQuery(id+"F0.imprint","IMPRINT",EDGE,{"disambiguationData":[TD([[makeQuery(id+"F0.imprint","INTERSECT",VERTEX,{"disambiguationData":[OD(1.0)],"derivedFrom":[subQ0,sQuery(id+"F0.wireOp",EDGE,"E7")]}),-1.0]])],"derivedFrom":subQ0})])],"isStart":true});}
            var Q10;
            Q10=makeQuery(id+"F1.opExtrude","CAP_EDGE",EDGE,{"disambiguationData":[OSD([sQuery(id+"F0.wireOp",EDGE,"E7")])],"isStart":true});
            var Q11;
            {var subQ0=sQuery(id+"F0.wireOp",EDGE,"E2.2");Q11=makeQuery(id+"F1.opExtrude","CAP_EDGE",EDGE,{"disambiguationData":[OSD([subQ0]),TDD([makeQuery(id+"F0.imprint","IMPRINT",EDGE,{"disambiguationData":[TD([[makeQuery(id+"F0.imprint","INTERSECT",VERTEX,{"disambiguationData":[OD(0.0)],"derivedFrom":[subQ0,sQuery(id+"F0.wireOp",EDGE,"E7")]}),1.0]])],"derivedFrom":subQ0})])],"isStart":true});}
            fillet(context, id + "F4", {"entities" : qUnion([Q0, Q1, Q2, Q3, Q4, Q5, Q6, Q7, Q8, Q9, Q10, Q11]), "radius" : 3 * mm, "tangentPropagation" : true, "allowEdgeOverflow" : false});
        }
    });
